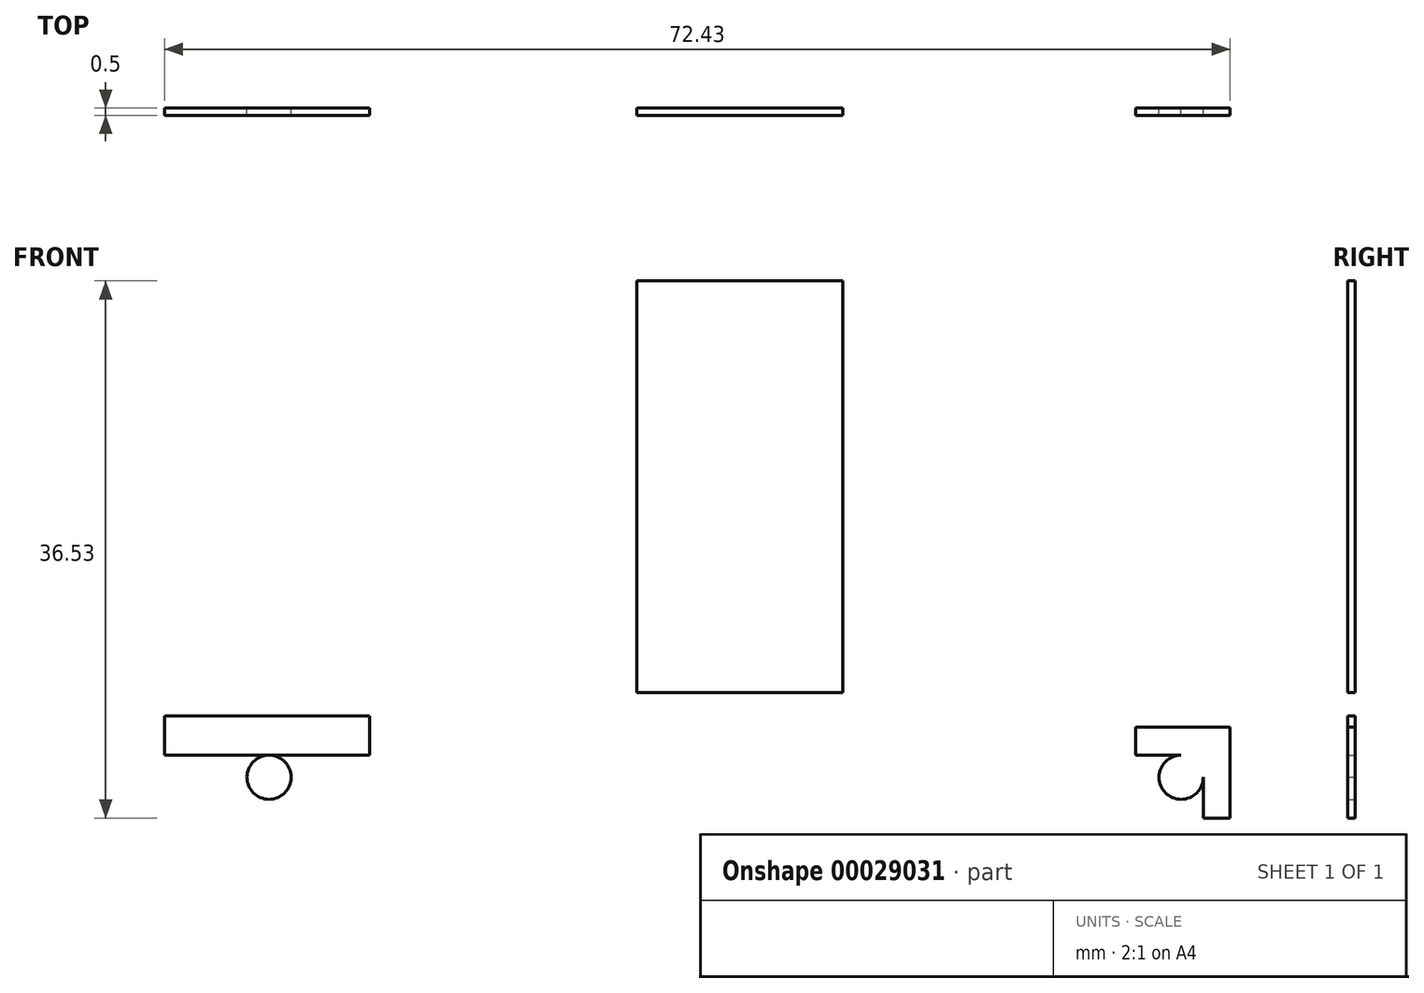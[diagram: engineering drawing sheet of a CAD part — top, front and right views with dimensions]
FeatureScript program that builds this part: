
annotation { "Feature Type Name" : "Feature", "Feature Type Description" : "" }
export const myFeature = defineFeature(function(context is Context, id is Id, definition is map)
    precondition{}
    {
        {
            var Q0;
            Q0=qCreatedBy(makeId("Front.planeOp"),FACE);
            var sketch = newSketch(context, id + "F0", { "sketchPlane" : qUnion([Q0])});
            skCircle(sketch, "E0", {"center": v(23, -33.75) * mm, "radius": 1.5 * mm});
            skCircle(sketch, "E1", {"center": v(-39, -33.75) * mm, "radius": 1.5 * mm});
            skLineSegment(sketch, "E2", {"start": v(24.5, -36.53) * mm, "end": v(24.5, -32.25) * mm});
            skLineSegment(sketch, "E3", {"start": v(24.5, -32.25) * mm, "end": v(19.9, -32.25) * mm});
            skLineSegment(sketch, "E4", {"start": v(19.9, -32.25) * mm, "end": v(19.9, -30.34) * mm});
            skLineSegment(sketch, "E5", {"start": v(19.9, -30.34) * mm, "end": v(26.32, -30.34) * mm});
            skLineSegment(sketch, "E6", {"start": v(26.32, -30.34) * mm, "end": v(26.32, -36.53) * mm});
            skLineSegment(sketch, "E7", {"start": v(26.32, -36.53) * mm, "end": v(24.5, -36.53) * mm});
            skLineSegment(sketch, "E8.bottom", {"start": v(-46.11, -29.6) * mm, "end": v(-32.17, -29.6) * mm});
            skLineSegment(sketch, "E8.top", {"start": v(-46.11, -32.25) * mm, "end": v(-32.17, -32.25) * mm});
            skLineSegment(sketch, "E8.left", {"start": v(-46.11, -29.6) * mm, "end": v(-46.11, -32.25) * mm});
            skLineSegment(sketch, "E8.right", {"start": v(-32.17, -29.6) * mm, "end": v(-32.17, -32.25) * mm});
            skLineSegment(sketch, "E9.bottom", {"start": v(0, 0) * mm, "end": v(-14, 0) * mm});
            skLineSegment(sketch, "E9.top", {"start": v(0, -28) * mm, "end": v(-14, -28) * mm});
            skLineSegment(sketch, "E9.left", {"start": v(0, 0) * mm, "end": v(0, -28) * mm});
            skLineSegment(sketch, "E9.right", {"start": v(-14, 0) * mm, "end": v(-14, -28) * mm});
            skLineSegment(sketch, "E10", {"start": v(-10.45, -6.4) * mm, "end": v(-2.77, -6.4) * mm});
            skLineSegment(sketch, "E11", {"start": v(-7, -2.64) * mm, "end": v(-7, -9.95) * mm});
            skSolve(sketch);
        }
        {
            var Q0;
            Q0 = qSketchRegion(id + "F0", true);
            extrude(context, id + "F1", {"entities" : qUnion([Q0]), "depth" : .5 * mm});
        }
    });
